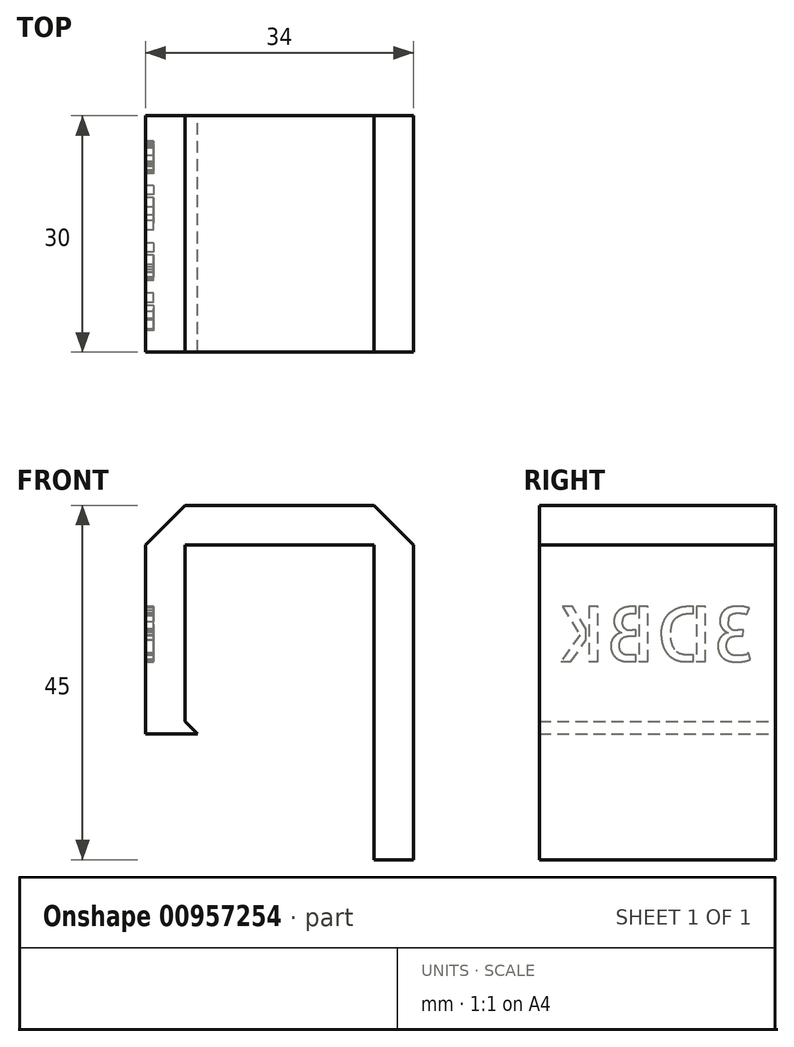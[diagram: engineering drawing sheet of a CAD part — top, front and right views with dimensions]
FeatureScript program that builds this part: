
annotation { "Feature Type Name" : "Feature", "Feature Type Description" : "" }
export const myFeature = defineFeature(function(context is Context, id is Id, definition is map)
    precondition{}
    {
        {
            var Q0;
            Q0=qCreatedBy(makeId("Front.planeOp"),FACE);
            var sketch = newSketch(context, id + "F0", { "sketchPlane" : qUnion([Q0])});
            skLineSegment(sketch, "E0", {"start": v(5.38, 0) * mm, "end": v(29.38, 0) * mm});
            skLineSegment(sketch, "E1", {"start": v(29.38, 0) * mm, "end": v(29.38, -40) * mm});
            skLineSegment(sketch, "E2", {"start": v(34.38, 5) * mm, "end": v(34.38, -40) * mm});
            skLineSegment(sketch, "E3", {"start": v(34.38, 5) * mm, "end": v(5.38, 5) * mm});
            skLineSegment(sketch, "E4", {"start": v(5.38, 5) * mm, "end": v(0.38, 5) * mm});
            skLineSegment(sketch, "E5", {"start": v(5.38, 0) * mm, "end": v(5.38, -22.41) * mm});
            skLineSegment(sketch, "E6", {"start": v(29.38, -40) * mm, "end": v(34.38, -40) * mm});
            skLineSegment(sketch, "E7", {"start": v(0.38, 5) * mm, "end": v(0.38, 0) * mm});
            skLineSegment(sketch, "E8", {"start": v(0.38, 0) * mm, "end": v(0.38, -24) * mm});
            skLineSegment(sketch, "E9", {"start": v(0.38, -24) * mm, "end": v(6.97, -24) * mm});
            skLineSegment(sketch, "E10", {"start": v(5.38, -22.41) * mm, "end": v(6.97, -24) * mm});
            skSolve(sketch);
        }
        {
            var Q0;
            Q0=makeQuery(id+"F0.imprint","IMPRINT",FACE,{"disambiguationData":[TD([[makeQuery(id+"F0.imprint","IMPRINT",EDGE,{"derivedFrom":sQuery(id+"F0.wireOp",EDGE,"E0")}),1.0]])]});
            extrude(context, id + "F1", {"entities" : qUnion([Q0]), "depth" : 30 * mm, "offsetDistance" : 25 * mm});
        }
        {
            var Q0;
            Q0=makeQuery(id+"F1.opExtrude","SWEPT_EDGE",EDGE,{"disambiguationData":[OSD([sQuery(id+"F0.wireOp",EDGE,"E4"),sQuery(id+"F0.wireOp",EDGE,"E7")])]});
            var Q1;
            Q1=makeQuery(id+"F1.opExtrude","SWEPT_EDGE",EDGE,{"disambiguationData":[OSD([sQuery(id+"F0.wireOp",EDGE,"E2"),sQuery(id+"F0.wireOp",EDGE,"E3")])]});
            chamfer(context, id + "F2", {"entities" : qUnion([Q0, Q1]), "width" : 5 * mm, "tangentPropagation" : true});
        }
        {
            var Q0;
            Q0=makeQuery(id+"F1.opExtrude","SWEPT_FACE",FACE,{"disambiguationData":[OSD([sQuery(id+"F0.wireOp",EDGE,"E7"),sQuery(id+"F0.wireOp",EDGE,"E8")])]});
            var sketch = newSketch(context, id + "F3", { "sketchPlane" : qUnion([Q0])});
            skText(sketch, "E11", { "text": "3DBK", "fontName": "AllertaStencil-Regular.ttf"});
            const initialGuessF3  = {"E11": [0.00248, -0.01484, 1, 0, 0.007]};
            skSetInitialGuess(sketch, initialGuessF3);
            skSolve(sketch);
        }
        {
            var Q0;
            Q0 = qSketchRegion(id + "F3", true);
            extrude(context, id + "F4", {"entities" : qUnion([Q0]), "operationType" : NewBodyOperationType.REMOVE, "oppositeDirection" : true, "depth" : 1 * mm, "offsetDistance" : 25 * mm});
        }
    });
